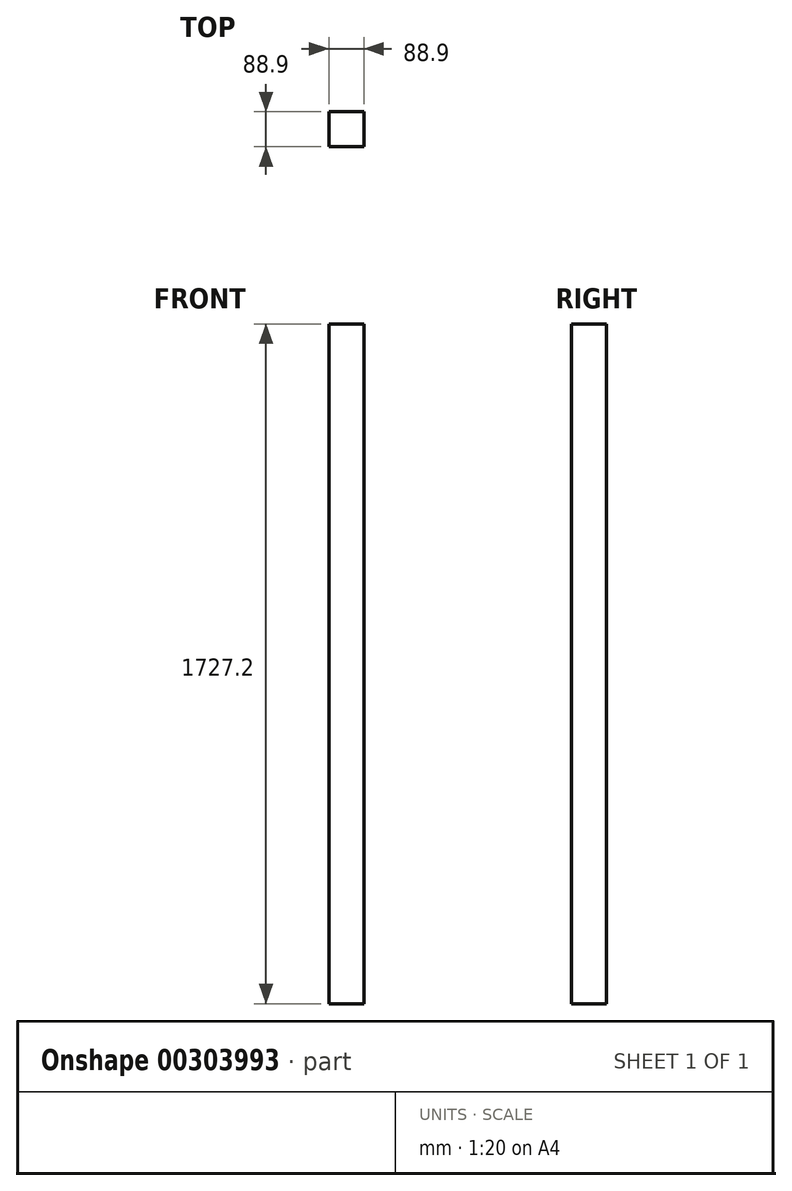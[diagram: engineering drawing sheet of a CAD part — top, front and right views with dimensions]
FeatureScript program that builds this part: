
annotation { "Feature Type Name" : "Feature", "Feature Type Description" : "" }
export const myFeature = defineFeature(function(context is Context, id is Id, definition is map)
    precondition{}
    {
        {
            var Q0;
            Q0=qCreatedBy(makeId("Top.planeOp"),FACE);
            var sketch = newSketch(context, id + "F0", { "sketchPlane" : qUnion([Q0])});
            skLineSegment(sketch, "E0.bottom", {"start": v(0, 0) * mm, "end": v(-88.9, 0) * mm});
            skLineSegment(sketch, "E0.top", {"start": v(0, -88.9) * mm, "end": v(-88.9, -88.9) * mm});
            skLineSegment(sketch, "E0.left", {"start": v(0, 0) * mm, "end": v(0, -88.9) * mm});
            skLineSegment(sketch, "E0.right", {"start": v(-88.9, 0) * mm, "end": v(-88.9, -88.9) * mm});
            skSolve(sketch);
        }
        {
            var Q0;
            Q0 = qSketchRegion(id + "F0", true);
            extrude(context, id + "F1", {"entities" : qUnion([Q0]), "depth" : 1727.2 * mm});
        }
    });
